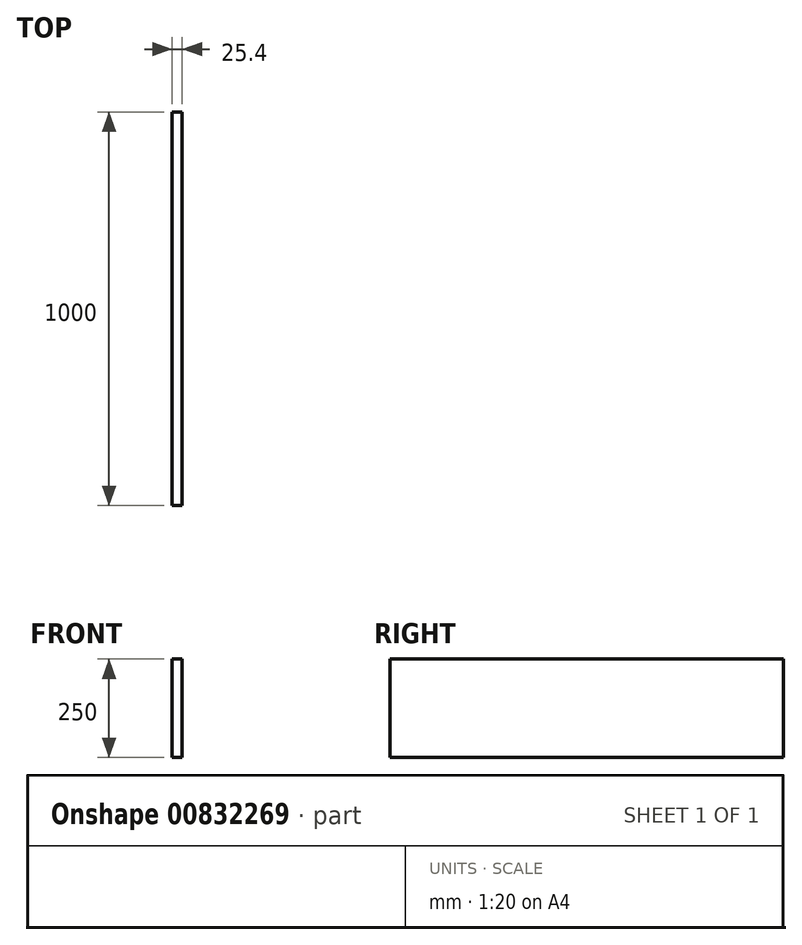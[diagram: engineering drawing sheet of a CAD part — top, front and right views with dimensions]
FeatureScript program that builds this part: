
annotation { "Feature Type Name" : "Feature", "Feature Type Description" : "" }
export const myFeature = defineFeature(function(context is Context, id is Id, definition is map)
    precondition{}
    {
        {
            var Q0;
            Q0=qCreatedBy(makeId("Right.planeOp"),FACE);
            var sketch = newSketch(context, id + "F0", { "sketchPlane" : qUnion([Q0])});
            skLineSegment(sketch, "E0.bottom", {"start": v(0, 0) * mm, "end": v(1000, 0) * mm});
            skLineSegment(sketch, "E0.top", {"start": v(0, 250) * mm, "end": v(1000, 250) * mm});
            skLineSegment(sketch, "E0.left", {"start": v(0, 0) * mm, "end": v(0, 250) * mm});
            skLineSegment(sketch, "E0.right", {"start": v(1000, 0) * mm, "end": v(1000, 250) * mm});
            skSolve(sketch);
        }
        {
            var Q0;
            Q0=makeQuery(id+"F0.imprint","IMPRINT",FACE,{"disambiguationData":[TD([[makeQuery(id+"F0.imprint","IMPRINT",EDGE,{"derivedFrom":sQuery(id+"F0.wireOp",EDGE,"E0.bottom")}),1.0]])]});
            extrude(context, id + "F1", {"entities" : qUnion([Q0]), "endBound" : BoundingType.SYMMETRIC, "depth" : 25.4 * mm, "offsetDistance" : 25.4 * mm});
        }
    });
